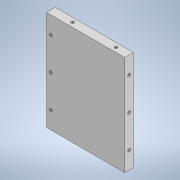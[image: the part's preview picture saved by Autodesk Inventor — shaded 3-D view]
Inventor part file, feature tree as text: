
AUTODESK INVENTOR PART (.ipt)
format: ipt  version: 2022.2 (Build 262287030, 287C)  size: 135,168 bytes
history: native  units: in
note: dims shown in document units (in); Inventor stores cm internally (conversion verified against a paired STEP export)
features: sketch x5, hole x4, extrude x1
ambient origin geometry x8: Origin, YZ Plane, XZ Plane, XY Plane, X Axis, Y Axis, Z Axis, Center Point
bodies: Solid1 (feature_tree)
feature tree (10):
  extrude  "Extrusion1"  Depth=4.5276in
  hole  "Hole1"  [1 undecoded]
  hole  "Hole2"  [1 undecoded]
  hole  "Hole3"  [1 undecoded]
  hole  "Hole4"  [1 undecoded]
  sketch  "Sketch1"  dims[d0=3.5433in d1=4.5276in]
  sketch  "Sketch2"  dims[d2=0.3937in d3=0.0in d4=0.7874in]
  sketch  "Sketch3"  dims[d5=0.1969in d6=1.1811in d8=1.4764in d9=0.3937in d11=0.3937in]
  sketch  "Sketch4"  dims[d13=0.125in d14=0.2953in d15=0.1476in d16=0.0984in d17=90.0deg d18=0.1969in d19=0.0in d20=0.9843in]
  sketch  "Sketch5"  dims[d21=0.1969in d22=0.7874in d24=1.9685in d25=0.3937in d27=0.3937in d29=0.125in d30=0.2953in d31=0.1476in d32=0.0984in d33=90.0deg d34=0.1969in d35=0.0in d36=0.9843in d37=0.1969in d38=0.7874in d40=1.9685in d41=0.3937in d43=0.3937in d45=0.125in d46=0.2953in d47=0.1476in d48=0.0984in d49=90.0deg d50=0.1969in d51=0.0in d52=0.1969in d53=0.7874in d54=1.1811in d56=1.4764in d57=0.3937in d59=0.3937in d61=0.125in d62=0.2953in d63=0.1476in d64=0.0984in d65=90.0deg d66=0.1969in d67=0.0in]
note: 4 required parameter values undecoded (feature->parameter linkage not recoverable at this tier; creation-order binding heuristic only, values carry confidence <= 0.55)
